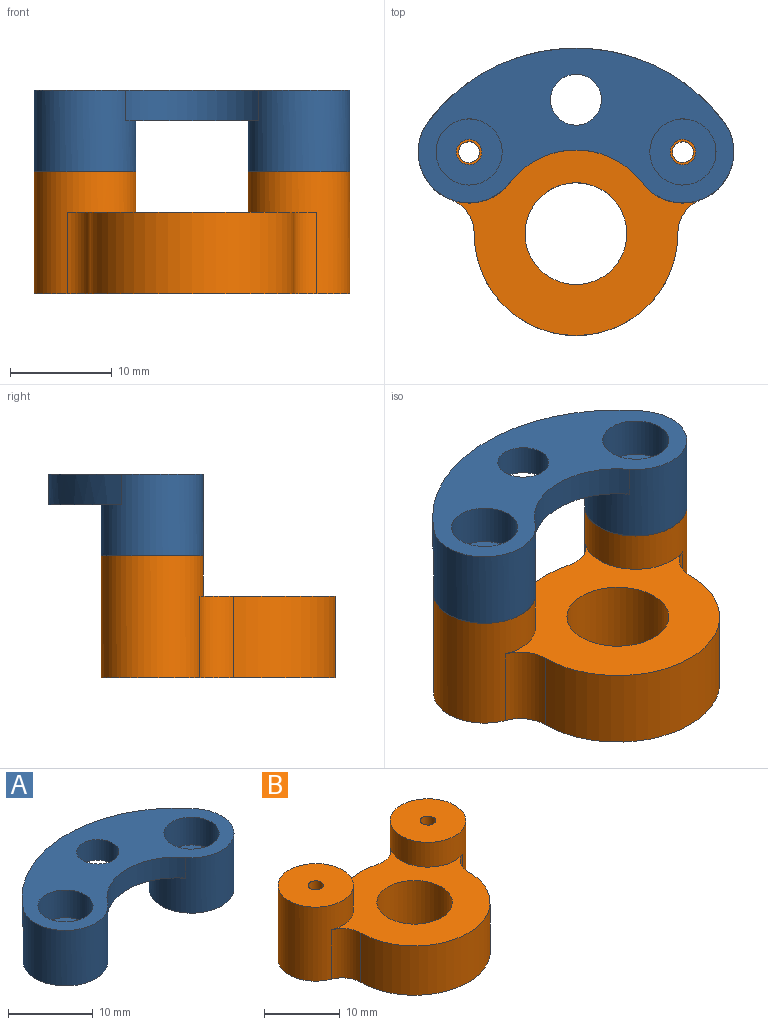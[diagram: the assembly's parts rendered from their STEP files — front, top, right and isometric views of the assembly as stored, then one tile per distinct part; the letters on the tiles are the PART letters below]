
ASSEMBLY  parts=2 mates=1
PART A: 15 faces, bbox 31x15.2x8 mm
  f0: cylinder r=1.25mm len=4mm, axis (0,0,-1), area 31.4mm2, adj f9,f12
  f1: cylinder r=1.25mm len=4mm, axis (0,0,-1), area 31.4mm2, adj f10,f14
  f2: cylinder r=5mm len=10mm, axis (0,0,-1), area 204.2mm2, adj f3,f6,f7,f8,f9
  f3: cylinder r=18.2mm len=28.95mm, axis (0,0,-1), area 100.4mm2, adj f2,f4,f7,f8
  f4: cylinder r=5mm len=10mm, axis (0,0,-1), area 204.2mm2, adj f3,f6,f7,f8,f10
  f5: cylinder r=2.5mm len=5mm, axis (0,0,-1), area 47.1mm2, adj f7,f8
  f6: cylinder r=8.2mm len=13.05mm, axis (0,0,-1), area 45.3mm2, adj f2,f4,f7,f8
  f7: plane 31x15.2mm, normal (0,0,1), area 235.4mm2, adj f2,f3,f4,f5,f6,f11,f13
  f8: plane 28.95x13.23mm, normal (0,0,-1), area 144.6mm2, adj f2,f3,f4,f5,f6
  f9: plane 10x10mm, normal (0,0,-1), area 73.6mm2, adj f0,f2
  f10: plane 10x10mm, normal (0,0,-1), area 73.6mm2, adj f1,f4
  f11: cylinder r=3.25mm len=6.5mm, axis (0,0,1), area 81.7mm2, adj f7,f12
  f12: plane 6.5x6.5mm, normal (0,0,1), area 28.3mm2, adj f0,f11
  f13: cylinder r=3.25mm len=6.5mm, axis (0,0,1), area 81.7mm2, adj f7,f14
  f14: plane 6.5x6.5mm, normal (0,0,1), area 28.3mm2, adj f1,f13
PART B: 15 faces, bbox 31x23x12 mm
  f0: plane 24.53x20.94mm, normal (0,0,1), area 227.4mm2, adj f1,f2,f3,f5,f6,f11,f12,f13
  f1: cylinder r=5mm len=12mm, axis (0,0,-1), area 274.6mm2, adj f0,f8,f10,f11,f12
  f2: cylinder r=10mm len=20mm, axis (0,0,-1), area 251.9mm2, adj f0,f8,f12,f14
  f3: cylinder r=5mm len=12mm, axis (0,0,-1), area 274.6mm2, adj f0,f8,f9,f13,f14
  f4: cylinder r=1.03mm len=12mm, axis (0,0,-1), area 77.3mm2, adj f8,f9
  f5: cylinder r=5mm len=10mm, axis (0,0,-1), area 251.3mm2, adj f0,f8
  f6: cylinder r=10mm len=8mm, axis (0,0,-1), area 43.5mm2, adj f0,f8,f11,f13
  f7: cylinder r=1.03mm len=12mm, axis (0,0,-1), area 77.3mm2, adj f8,f10
  f8: plane 31x23mm, normal (0,0,-1), area 377.8mm2, adj f1,f2,f3,f4,f5,f6,f7,f11
  f9: plane 10x10mm, normal (0,0,1), area 75.2mm2, adj f3,f4
  f10: plane 10x10mm, normal (0,0,1), area 75.2mm2, adj f1,f7
  f11: cylinder r=3.5mm len=8mm, axis (0,0,1), area 34mm2, adj f0,f1,f6,f8
  f12: cylinder r=3.5mm len=8mm, axis (0,0,1), area 34mm2, adj f0,f1,f2,f8
  f13: cylinder r=3.5mm len=8mm, axis (0,0,1), area 34mm2, adj f0,f3,f6,f8
  f14: cylinder r=3.5mm len=8mm, axis (0,0,1), area 34mm2, adj f0,f2,f3,f8
PLACE A at identity
PLACE B t=(-18.19,-43.98,-17)mm
MATE fastened B.f3 <-> A.f0  axis (0,0,1) through (-40.78,-9.03,-5)mm
